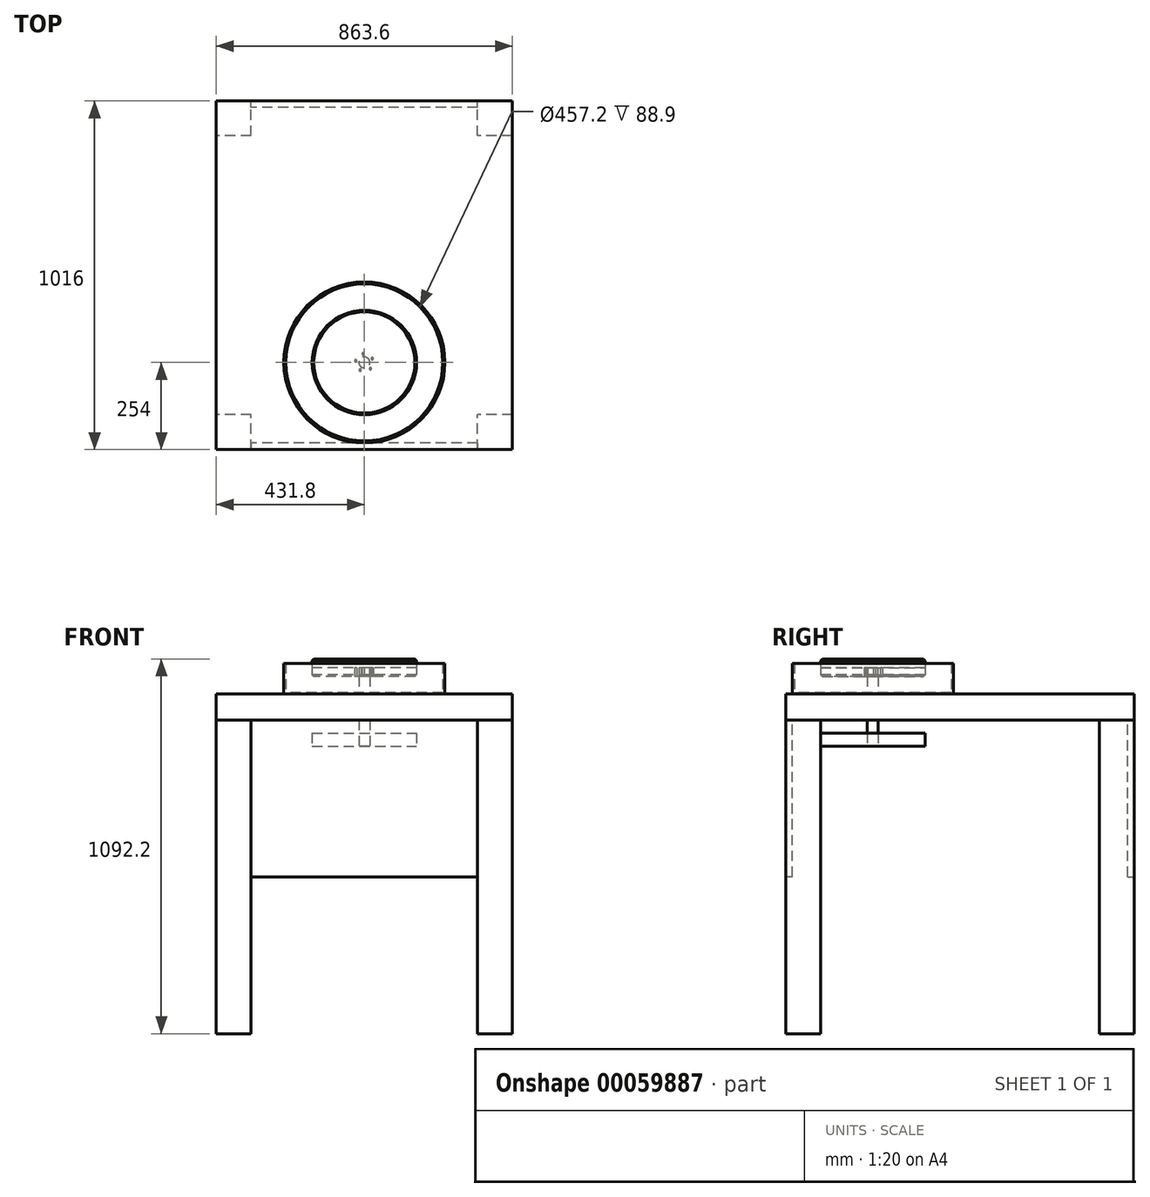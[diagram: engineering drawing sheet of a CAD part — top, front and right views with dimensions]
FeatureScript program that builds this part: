
annotation { "Feature Type Name" : "Feature", "Feature Type Description" : "" }
export const myFeature = defineFeature(function(context is Context, id is Id, definition is map)
    precondition{}
    {
        {
            var Q0;
            Q0=qCreatedBy(makeId("Top.planeOp"),FACE);
            var sketch = newSketch(context, id + "F0", { "sketchPlane" : qUnion([Q0])});
            skLineSegment(sketch, "E0.rect.bottom", {"start": v(381, -457.2) * mm, "end": v(-381, -457.2) * mm, "construction": true});
            skLineSegment(sketch, "E0.rect.top", {"start": v(381, 457.2) * mm, "end": v(-381, 457.2) * mm, "construction": true});
            skLineSegment(sketch, "E0.rect.left", {"start": v(381, -457.2) * mm, "end": v(381, 457.2) * mm, "construction": true});
            skLineSegment(sketch, "E0.rect.right", {"start": v(-381, -457.2) * mm, "end": v(-381, 457.2) * mm, "construction": true});
            skPoint(sketch, "E0.rect.middle", {"position": v(0, 0) * mm});
            skLineSegment(sketch, "E1.rect.bottom", {"start": v(-330.2, 406.4) * mm, "end": v(-431.8, 406.4) * mm});
            skLineSegment(sketch, "E1.rect.top", {"start": v(-330.2, 508) * mm, "end": v(-431.8, 508) * mm});
            skLineSegment(sketch, "E1.rect.left", {"start": v(-330.2, 406.4) * mm, "end": v(-330.2, 508) * mm});
            skLineSegment(sketch, "E1.rect.right", {"start": v(-431.8, 406.4) * mm, "end": v(-431.8, 508) * mm});
            skPoint(sketch, "E1.rect.middle", {"position": v(-381, 457.2) * mm});
            skLineSegment(sketch, "E2.rect.bottom", {"start": v(431.8, 406.4) * mm, "end": v(330.2, 406.4) * mm});
            skLineSegment(sketch, "E2.rect.top", {"start": v(431.8, 508) * mm, "end": v(330.2, 508) * mm});
            skLineSegment(sketch, "E2.rect.left", {"start": v(431.8, 406.4) * mm, "end": v(431.8, 508) * mm});
            skLineSegment(sketch, "E2.rect.right", {"start": v(330.2, 406.4) * mm, "end": v(330.2, 508) * mm});
            skPoint(sketch, "E2.rect.middle", {"position": v(381, 457.2) * mm});
            skLineSegment(sketch, "E3.rect.bottom", {"start": v(431.8, -508) * mm, "end": v(330.2, -508) * mm});
            skLineSegment(sketch, "E3.rect.top", {"start": v(431.8, -406.4) * mm, "end": v(330.2, -406.4) * mm});
            skLineSegment(sketch, "E3.rect.left", {"start": v(431.8, -508) * mm, "end": v(431.8, -406.4) * mm});
            skLineSegment(sketch, "E3.rect.right", {"start": v(330.2, -508) * mm, "end": v(330.2, -406.4) * mm});
            skPoint(sketch, "E3.rect.middle", {"position": v(381, -457.2) * mm});
            skLineSegment(sketch, "E4.rect.bottom", {"start": v(-330.2, -508) * mm, "end": v(-431.8, -508) * mm});
            skLineSegment(sketch, "E4.rect.top", {"start": v(-330.2, -406.4) * mm, "end": v(-431.8, -406.4) * mm});
            skLineSegment(sketch, "E4.rect.left", {"start": v(-330.2, -508) * mm, "end": v(-330.2, -406.4) * mm});
            skLineSegment(sketch, "E4.rect.right", {"start": v(-431.8, -508) * mm, "end": v(-431.8, -406.4) * mm});
            skPoint(sketch, "E4.rect.middle", {"position": v(-381, -457.2) * mm});
            skPoint(sketch, "E4.rect.cornerSnap0", {"position": v(381, -508) * mm});
            skSolve(sketch);
        }
        {
            var Q0;
            Q0 = qSketchRegion(id + "F0", true);
            extrude(context, id + "F1", {"entities" : qUnion([Q0]), "depth" : 914.4 * mm});
        }
        {
            var Q0;
            Q0=makeQuery(id+"F1.opExtrude","CAP_FACE",FACE,{"disambiguationData":[OSD([sQuery(id+"F0.wireOp",EDGE,"E1.rect.bottom"),sQuery(id+"F0.wireOp",EDGE,"E1.rect.top"),sQuery(id+"F0.wireOp",EDGE,"E1.rect.left"),sQuery(id+"F0.wireOp",EDGE,"E1.rect.right")])],"isStart":false});
            var sketch = newSketch(context, id + "F2", { "sketchPlane" : qUnion([Q0])});
            skLineSegment(sketch, "E5.rect.bottom", {"start": v(-431.8, 508) * mm, "end": v(431.8, 508) * mm});
            skLineSegment(sketch, "E5.rect.top", {"start": v(-431.8, -508) * mm, "end": v(431.8, -508) * mm});
            skLineSegment(sketch, "E5.rect.left", {"start": v(-431.8, 508) * mm, "end": v(-431.8, -508) * mm});
            skLineSegment(sketch, "E5.rect.right", {"start": v(431.8, 508) * mm, "end": v(431.8, -508) * mm});
            skPoint(sketch, "E5.rect.middle", {"position": v(0, 0) * mm});
            skSolve(sketch);
        }
        {
            var Q0;
            Q0 = qSketchRegion(id + "F2", true);
            extrude(context, id + "F3", {"entities" : qUnion([Q0]), "depth" : 76.2 * mm});
        }
        {
            var Q0;
            Q0=makeQuery(id+"F3.opExtrude","CAP_FACE",FACE,{"disambiguationData":[OSD([sQuery(id+"F2.wireOp",EDGE,"E5.rect.bottom"),sQuery(id+"F2.wireOp",EDGE,"E5.rect.top"),sQuery(id+"F2.wireOp",EDGE,"E5.rect.left"),sQuery(id+"F2.wireOp",EDGE,"E5.rect.right")])],"isStart":false});
            var sketch = newSketch(context, id + "F4", { "sketchPlane" : qUnion([Q0])});
            skCircle(sketch, "E6", {"center": v(0, -254) * mm, "radius": 12.7 * mm});
            skSolve(sketch);
        }
        {
            var Q0;
            Q0=sQuery(id+"F4.wireOp",VERTEX,"E6.center");
            var Q1;
            Q1=makeQuery(id+"F3.opExtrude","SWEPT_BODY",BODY,{"disambiguationData":[OSD([sQuery(id+"F2.wireOp",EDGE,"E5.rect.bottom"),sQuery(id+"F2.wireOp",EDGE,"E5.rect.top"),sQuery(id+"F2.wireOp",EDGE,"E5.rect.left"),sQuery(id+"F2.wireOp",EDGE,"E5.rect.right")])]});
            hole(context, id + "F5", {"style" : HoleStyle.SIMPLE, "holeDiameter" : 31.75 * mm, "endStyle" : HoleEndStyle.THROUGH, "locations" : qUnion([Q0]), "scope" : qUnion([Q1])});
        }
        {
            var Q0;
            Q0=makeQuery(id+"F3.opExtrude","CAP_FACE",FACE,{"disambiguationData":[OSD([sQuery(id+"F2.wireOp",EDGE,"E5.rect.bottom"),sQuery(id+"F2.wireOp",EDGE,"E5.rect.top"),sQuery(id+"F2.wireOp",EDGE,"E5.rect.left"),sQuery(id+"F2.wireOp",EDGE,"E5.rect.right")])],"isStart":false});
            var sketch = newSketch(context, id + "F6", { "sketchPlane" : qUnion([Q0])});
            skCircle(sketch, "E7.0", {"center": v(0, -254) * mm, "radius": 15.88 * mm});
            skSolve(sketch);
        }
        {
            var Q0;
            Q0 = qSketchRegion(id + "F6", true);
            extrude(context, id + "F7", {"entities" : qUnion([Q0]), "operationType" : NewBodyOperationType.ADD, "depth" : 50.8 * mm, "hasSecondDirection" : true, "secondDirectionOppositeDirection" : true, "secondDirectionDepth" : 152.4 * mm});
        }
        {
            var Q0;
            Q0=makeQuery(id+"F7.opExtrude","CAP_FACE",FACE,{"disambiguationData":[OSD([sQuery(id+"F6.wireOp",EDGE,"E7.0")])],"isStart":false});
            var sketch = newSketch(context, id + "F8", { "sketchPlane" : qUnion([Q0])});
            skCircle(sketch, "E8", {"center": v(0, -254) * mm, "radius": 152.4 * mm});
            skCircle(sketch, "E9", {"center": v(-24.99, -249.44) * mm, "radius": 3.18 * mm});
            skCircle(sketch, "E10.1.0", {"center": v(-12.06, -276.36) * mm, "radius": 3.18 * mm});
            skCircle(sketch, "E10.2.0", {"center": v(17.53, -272.38) * mm, "radius": 3.18 * mm});
            skLineSegment(sketch, "E10.anchor1", {"start": v(0, -254) * mm, "end": v(-24.99, -249.44) * mm, "construction": true});
            skLineSegment(sketch, "E10.anchor2", {"start": v(0, -254) * mm, "end": v(-3.38, -228.83) * mm, "construction": true});
            skCircle(sketch, "E11.1.3.0", {"center": v(22.9, -243) * mm, "radius": 3.18 * mm});
            skCircle(sketch, "E11.1.4.0", {"center": v(-3.38, -228.83) * mm, "radius": 3.18 * mm});
            skSolve(sketch);
        }
        {
            var Q0;
            Q0 = qSketchRegion(id + "F8", true);
            extrude(context, id + "F9", {"entities" : qUnion([Q0]), "operationType" : NewBodyOperationType.ADD, "depth" : 25.4 * mm});
        }
        {
            var Q0;
            Q0=makeQuery(id+"F9.opExtrude","CAP_FACE",FACE,{"disambiguationData":[OSD([sQuery(id+"F8.wireOp",EDGE,"E8"),sQuery(id+"F8.wireOp",EDGE,"E9"),sQuery(id+"F8.wireOp",EDGE,"E10.1.0"),sQuery(id+"F8.wireOp",EDGE,"E10.2.0"),sQuery(id+"F8.wireOp",EDGE,"E11.1.3.0"),sQuery(id+"F8.wireOp",EDGE,"E11.1.4.0")])],"isStart":false});
            var sketch = newSketch(context, id + "F10", { "sketchPlane" : qUnion([Q0])});
            skCircle(sketch, "E12.0", {"center": v(0, -254) * mm, "radius": 152.4 * mm});
            skSolve(sketch);
        }
        {
            var Q0;
            Q0 = qSketchRegion(id + "F10", true);
            extrude(context, id + "F11", {"entities" : qUnion([Q0]), "depth" : 25.4 * mm});
        }
        {
            var Q0;
            Q0=makeQuery(id+"F11.opExtrude","CAP_EDGE",EDGE,{"disambiguationData":[OSD([sQuery(id+"F10.wireOp",EDGE,"E12.0")])],"isStart":false});
            var Q1;
            Q1=makeQuery(id+"F9.opExtrude","CAP_EDGE",EDGE,{"disambiguationData":[OSD([sQuery(id+"F8.wireOp",EDGE,"E8")])],"isStart":true});
            chamfer(context, id + "F12", {"entities" : qUnion([Q0, Q1]), "width" : 5.08 * mm, "tangentPropagation" : true});
        }
        {
            var Q0;
            Q0=makeQuery(id+"F3.opExtrude","CAP_FACE",FACE,{"disambiguationData":[OSD([sQuery(id+"F2.wireOp",EDGE,"E5.rect.bottom"),sQuery(id+"F2.wireOp",EDGE,"E5.rect.top"),sQuery(id+"F2.wireOp",EDGE,"E5.rect.left"),sQuery(id+"F2.wireOp",EDGE,"E5.rect.right")])],"isStart":false});
            var sketch = newSketch(context, id + "F13", { "sketchPlane" : qUnion([Q0])});
            skCircle(sketch, "E13", {"center": v(0, -254) * mm, "radius": 228.6 * mm});
            skCircle(sketch, "E14.0", {"center": v(0, -254) * mm, "radius": 234.95 * mm});
            skSolve(sketch);
        }
        {
            var Q0;
            Q0 = qSketchRegion(id + "F13", true);
            extrude(context, id + "F14", {"entities" : qUnion([Q0]), "depth" : 88.9 * mm});
        }
        {
            var Q0;
            Q0=makeQuery(id+"F3.opExtrude","CAP_FACE",FACE,{"disambiguationData":[OSD([sQuery(id+"F2.wireOp",EDGE,"E5.rect.bottom"),sQuery(id+"F2.wireOp",EDGE,"E5.rect.top"),sQuery(id+"F2.wireOp",EDGE,"E5.rect.left"),sQuery(id+"F2.wireOp",EDGE,"E5.rect.right")])],"isStart":false});
            var sketch = newSketch(context, id + "F15", { "sketchPlane" : qUnion([Q0])});
            skCircle(sketch, "E15.0", {"center": v(0, -254) * mm, "radius": 228.6 * mm});
            skSolve(sketch);
        }
        {
            var Q0;
            Q0 = qSketchRegion(id + "F15", true);
            extrude(context, id + "F16", {"entities" : qUnion([Q0]), "depth" : 3.17 * mm});
        }
        {
            var Q0;
            Q0=makeQuery(id+"F7.opExtrude","CAP_FACE",FACE,{"disambiguationData":[OSD([sQuery(id+"F6.wireOp",EDGE,"E7.0")])],"isStart":true});
            var sketch = newSketch(context, id + "F17", { "sketchPlane" : qUnion([Q0])});
            skCircle(sketch, "E16", {"center": v(0, 254) * mm, "radius": 152.4 * mm});
            skSolve(sketch);
        }
        {
            var Q0;
            Q0 = qSketchRegion(id + "F17", true);
            extrude(context, id + "F18", {"entities" : qUnion([Q0]), "oppositeDirection" : true, "depth" : 38.1 * mm});
        }
        {
            var Q0;
            Q0=makeQuery(id+"F3.opExtrude","CAP_FACE",FACE,{"disambiguationData":[OSD([sQuery(id+"F2.wireOp",EDGE,"E5.rect.bottom"),sQuery(id+"F2.wireOp",EDGE,"E5.rect.top"),sQuery(id+"F2.wireOp",EDGE,"E5.rect.left"),sQuery(id+"F2.wireOp",EDGE,"E5.rect.right")])],"isStart":true});
            var sketch = newSketch(context, id + "F19", { "sketchPlane" : qUnion([Q0])});
            skLineSegment(sketch, "E17.bottom", {"start": v(330.2, -488.95) * mm, "end": v(-330.2, -488.95) * mm});
            skLineSegment(sketch, "E17.top", {"start": v(330.2, -508) * mm, "end": v(-330.2, -508) * mm});
            skLineSegment(sketch, "E17.left", {"start": v(330.2, -488.95) * mm, "end": v(330.2, -508) * mm});
            skLineSegment(sketch, "E17.right", {"start": v(-330.2, -488.95) * mm, "end": v(-330.2, -508) * mm});
            skSolve(sketch);
        }
        {
            var Q0;
            Q0 = qSketchRegion(id + "F19", true);
            extrude(context, id + "F20", {"entities" : qUnion([Q0]), "depth" : 457.2 * mm});
        }
        {
            var Q0;
            Q0=makeQuery(id+"F20.opExtrude","SWEPT_BODY",BODY,{"disambiguationData":[OSD([sQuery(id+"F19.wireOp",EDGE,"E17.bottom"),sQuery(id+"F19.wireOp",EDGE,"E17.top"),sQuery(id+"F19.wireOp",EDGE,"E17.left"),sQuery(id+"F19.wireOp",EDGE,"E17.right")])]});
            var Q1;
            Q1=qCreatedBy(makeId("Front.planeOp"),FACE);
            mirror(context, id + "F21", {"entities" : qUnion([Q0]), "mirrorPlane" : qUnion([Q1])});
        }
    });
